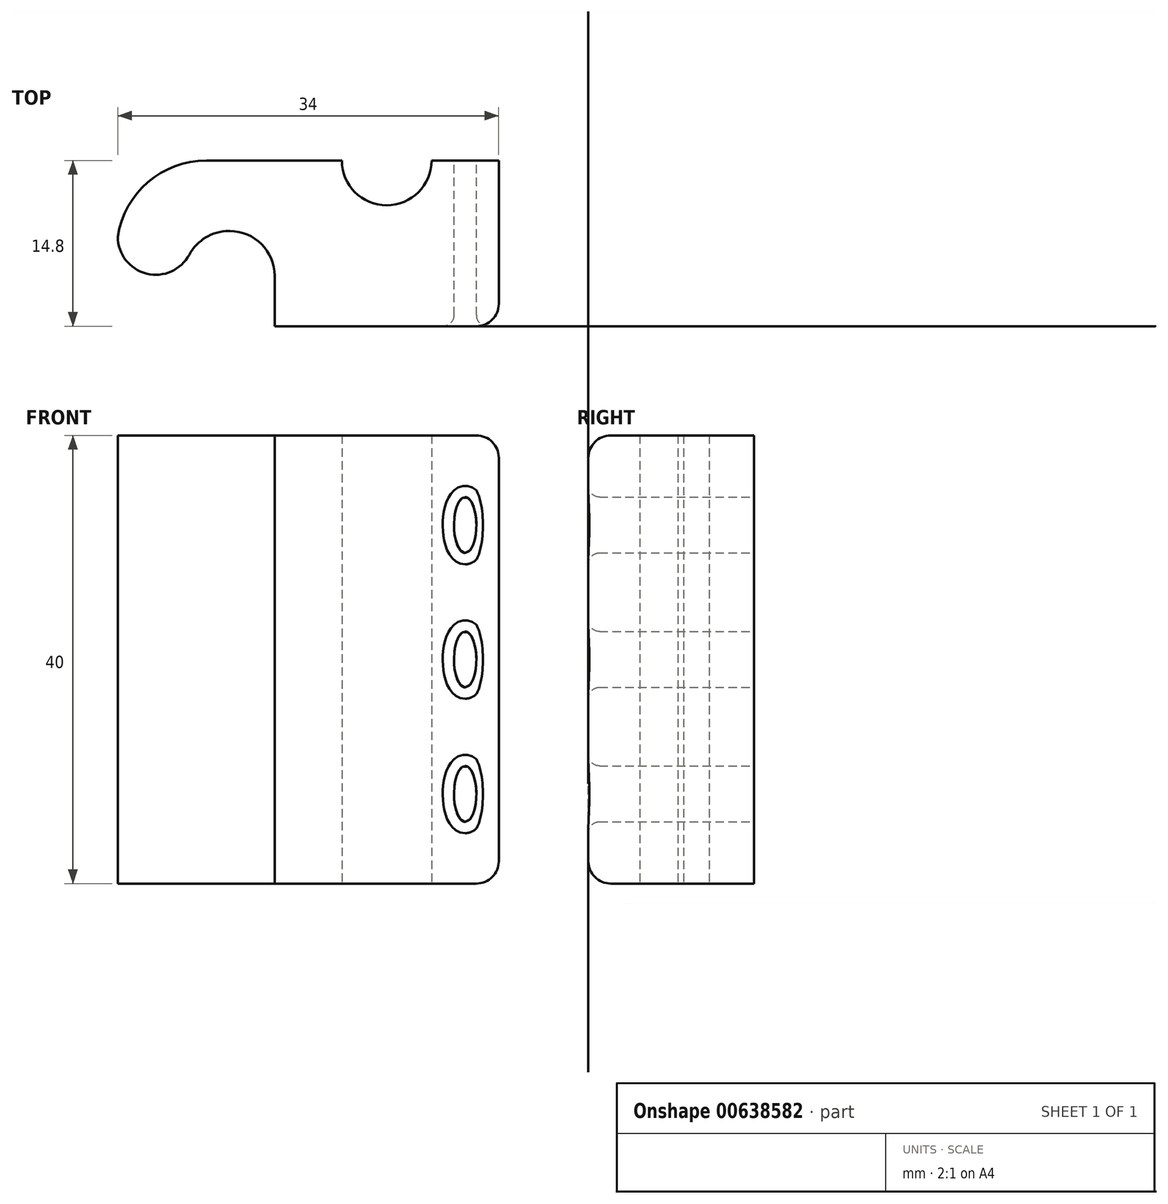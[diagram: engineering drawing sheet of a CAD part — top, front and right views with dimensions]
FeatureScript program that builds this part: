
annotation { "Feature Type Name" : "Feature", "Feature Type Description" : "" }
export const myFeature = defineFeature(function(context is Context, id is Id, definition is map)
    precondition{}
    {
        {
            var Q0;
            Q0=qCreatedBy(makeId("Top.planeOp"),FACE);
            var sketch = newSketch(context, id + "F0", { "sketchPlane" : qUnion([Q0])});
            skArc(sketch, "E0", {"start": v(-48.92, -31.37) * mm, "mid": v(-45.52, -34.77) * mm, "end": v(-42.12, -31.37) * mm});
            skLineSegment(sketch, "E1", {"start": v(-48.92, -31.37) * mm, "end": v(-48.92, -24.57) * mm});
            skLineSegment(sketch, "E2", {"start": v(-48.92, -24.57) * mm, "end": v(-28.92, -24.57) * mm});
            skArc(sketch, "E3", {"start": v(-28.92, -24.57) * mm, "mid": v(-24.92, -28.57) * mm, "end": v(-20.92, -24.57) * mm});
            skLineSegment(sketch, "E4", {"start": v(-20.92, -24.57) * mm, "end": v(-14.92, -24.57) * mm});
            skLineSegment(sketch, "E5", {"start": v(-14.92, -24.57) * mm, "end": v(-14.92, -39.37) * mm});
            skLineSegment(sketch, "E6", {"start": v(-14.92, -39.37) * mm, "end": v(-34.92, -39.37) * mm});
            skLineSegment(sketch, "E7", {"start": v(-34.92, -39.37) * mm, "end": v(-34.92, -31.37) * mm});
            skLineSegment(sketch, "E8.top", {"start": v(-34.92, -30.87) * mm, "end": v(-42.12, -30.87) * mm});
            skLineSegment(sketch, "E8.left", {"start": v(-34.92, -31.37) * mm, "end": v(-34.92, -30.87) * mm});
            skLineSegment(sketch, "E8.right", {"start": v(-42.12, -31.37) * mm, "end": v(-42.12, -30.87) * mm});
            skSolve(sketch);
        }
        {
            var Q0;
            Q0=makeQuery(id+"F0.imprint","IMPRINT",FACE,{"disambiguationData":[TD([[makeQuery(id+"F0.imprint","IMPRINT",EDGE,{"derivedFrom":sQuery(id+"F0.wireOp",EDGE,"E0")}),1.0]])]});
            extrude(context, id + "F1", {"entities" : qUnion([Q0]), "depth" : 40 * mm, "offsetDistance" : 25 * mm});
        }
        {
            var Q0;
            Q0=makeQuery(id+"F1.opExtrude","CAP_EDGE",EDGE,{"disambiguationData":[OSD([sQuery(id+"F0.wireOp",EDGE,"E6")])],"isStart":false});
            var Q1;
            Q1=makeQuery(id+"F1.opExtrude","CAP_EDGE",EDGE,{"disambiguationData":[OSD([sQuery(id+"F0.wireOp",EDGE,"E5")])],"isStart":false});
            var Q2;
            Q2=makeQuery(id+"F1.opExtrude","CAP_EDGE",EDGE,{"disambiguationData":[OSD([sQuery(id+"F0.wireOp",EDGE,"E5")])],"isStart":true});
            var Q3;
            Q3=makeQuery(id+"F1.opExtrude","CAP_EDGE",EDGE,{"disambiguationData":[OSD([sQuery(id+"F0.wireOp",EDGE,"E6")])],"isStart":true});
            fillet(context, id + "F2", {"entities" : qUnion([Q0, Q1, Q2, Q3]), "radius" : 2 * mm, "tangentPropagation" : true, "allowEdgeOverflow" : false});
        }
        {
            var Q0;
            Q0=makeQuery(id+"F1.opExtrude","SWEPT_EDGE",EDGE,{"disambiguationData":[OSD([sQuery(id+"F0.wireOp",EDGE,"E1"),sQuery(id+"F0.wireOp",EDGE,"E2")])]});
            fillet(context, id + "F3", {"entities" : qUnion([Q0]), "radius" : 8 * mm, "tangentPropagation" : true, "allowEdgeOverflow" : false});
        }
        {
            var Q0;
            Q0=makeQuery(id+"F1.opExtrude","SWEPT_EDGE",EDGE,{"disambiguationData":[OSD([sQuery(id+"F0.wireOp",EDGE,"E8.top"),sQuery(id+"F0.wireOp",EDGE,"E8.right")])]});
            var Q1;
            Q1=makeQuery(id+"F1.opExtrude","SWEPT_EDGE",EDGE,{"disambiguationData":[OSD([sQuery(id+"F0.wireOp",EDGE,"E8.top"),sQuery(id+"F0.wireOp",EDGE,"E8.left")])]});
            fillet(context, id + "F4", {"entities" : qUnion([Q0, Q1]), "radius" : 4 * mm, "tangentPropagation" : true, "allowEdgeOverflow" : false});
        }
        {
            var Q0;
            Q0=qCreatedBy(makeId("Front.planeOp"),FACE);
            var sketch = newSketch(context, id + "F5", { "sketchPlane" : qUnion([Q0])});
            skEllipse(sketch, "E9", {"center": v(-17.92, 32) * mm, "majorRadius": 2.5 * mm, "minorRadius": 1 * mm, "majorAxis": v(0, -1)});
            skEllipse(sketch, "E10.1.0.0", {"center": v(-17.92, 20) * mm, "majorRadius": 2.5 * mm, "minorRadius": 1 * mm, "majorAxis": v(0, -1)});
            skEllipse(sketch, "E10.2.0.0", {"center": v(-17.92, 8) * mm, "majorRadius": 2.5 * mm, "minorRadius": 1 * mm, "majorAxis": v(0, -1)});
            skLineSegment(sketch, "E10.direction1", {"start": v(-17.92, 32) * mm, "end": v(-17.92, 20) * mm, "construction": true});
            skSolve(sketch);
        }
        {
            var Q0;
            Q0 = qSketchRegion(id + "F5", true);
            extrude(context, id + "F6", {"entities" : qUnion([Q0]), "operationType" : NewBodyOperationType.REMOVE, "endBound" : BoundingType.THROUGH_ALL, "depth" : 25 * mm, "offsetDistance" : 25 * mm});
        }
        {
            var Q0;
            Q0=makeQuery(id+"F6.boolean.opBoolean","INTERSECT",EDGE,{"derivedFrom":[makeQuery(id+"F1.opExtrude","SWEPT_FACE",FACE,{"disambiguationData":[OSD([sQuery(id+"F0.wireOp",EDGE,"E6")])]}),makeQuery(id+"F6.opExtrude","SWEPT_FACE",FACE,{"disambiguationData":[OSD([sQuery(id+"F5.wireOp",EDGE,"E9")])]})]});
            var Q1;
            Q1=makeQuery(id+"F6.boolean.opBoolean","INTERSECT",EDGE,{"derivedFrom":[makeQuery(id+"F1.opExtrude","SWEPT_FACE",FACE,{"disambiguationData":[OSD([sQuery(id+"F0.wireOp",EDGE,"E6")])]}),makeQuery(id+"F6.opExtrude","SWEPT_FACE",FACE,{"disambiguationData":[OSD([sQuery(id+"F5.wireOp",EDGE,"E10.1.0.0")])]})]});
            var Q2;
            Q2=makeQuery(id+"F6.boolean.opBoolean","INTERSECT",EDGE,{"derivedFrom":[makeQuery(id+"F1.opExtrude","SWEPT_FACE",FACE,{"disambiguationData":[OSD([sQuery(id+"F0.wireOp",EDGE,"E6")])]}),makeQuery(id+"F6.opExtrude","SWEPT_FACE",FACE,{"disambiguationData":[OSD([sQuery(id+"F5.wireOp",EDGE,"E10.2.0.0")])]})]});
            fillet(context, id + "F7", {"entities" : qUnion([Q0, Q1, Q2]), "radius" : 1 * mm, "tangentPropagation" : true, "allowEdgeOverflow" : false});
        }
        {
            var Q0;
            Q0=makeQuery(id+"F1.opExtrude","SWEPT_EDGE",EDGE,{"disambiguationData":[OSD([sQuery(id+"F0.wireOp",EDGE,"E5"),sQuery(id+"F0.wireOp",EDGE,"E6")])]});
            fillet(context, id + "F8", {"entities" : qUnion([Q0]), "radius" : 2 * mm, "tangentPropagation" : true, "allowEdgeOverflow" : false});
        }
    });
